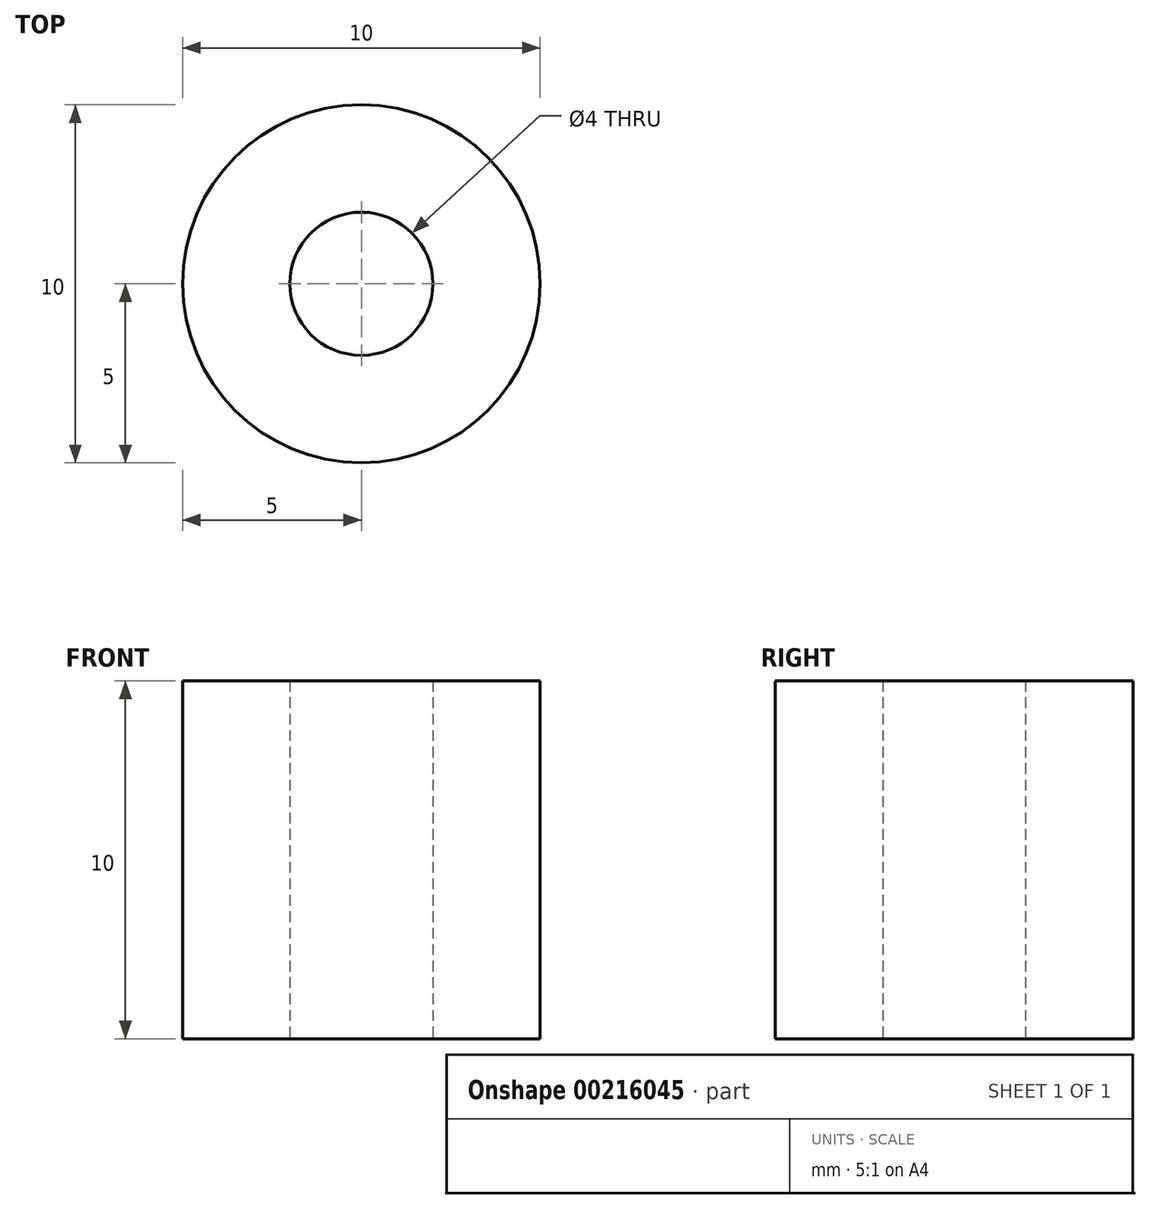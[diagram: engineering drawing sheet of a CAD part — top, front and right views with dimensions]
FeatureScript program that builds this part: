
annotation { "Feature Type Name" : "Feature", "Feature Type Description" : "" }
export const myFeature = defineFeature(function(context is Context, id is Id, definition is map)
    precondition{}
    {
        {
            var Q0;
            Q0=qCreatedBy(makeId("Top.planeOp"),FACE);
            var sketch = newSketch(context, id + "F0", { "sketchPlane" : qUnion([Q0])});
            skCircle(sketch, "E0", {"center": v(0, 0) * mm, "radius": 2 * mm});
            skCircle(sketch, "E1", {"center": v(0, 0) * mm, "radius": 5 * mm});
            skSolve(sketch);
        }
        {
            var Q0;
            Q0=makeQuery(id+"F0.imprint","IMPRINT",FACE,{"disambiguationData":[TD([[makeQuery(id+"F0.imprint","IMPRINT",EDGE,{"derivedFrom":sQuery(id+"F0.wireOp",EDGE,"E0")}),-1.0]])]});
            extrude(context, id + "F1", {"entities" : qUnion([Q0]), "depth" : 10 * mm});
        }
    });
